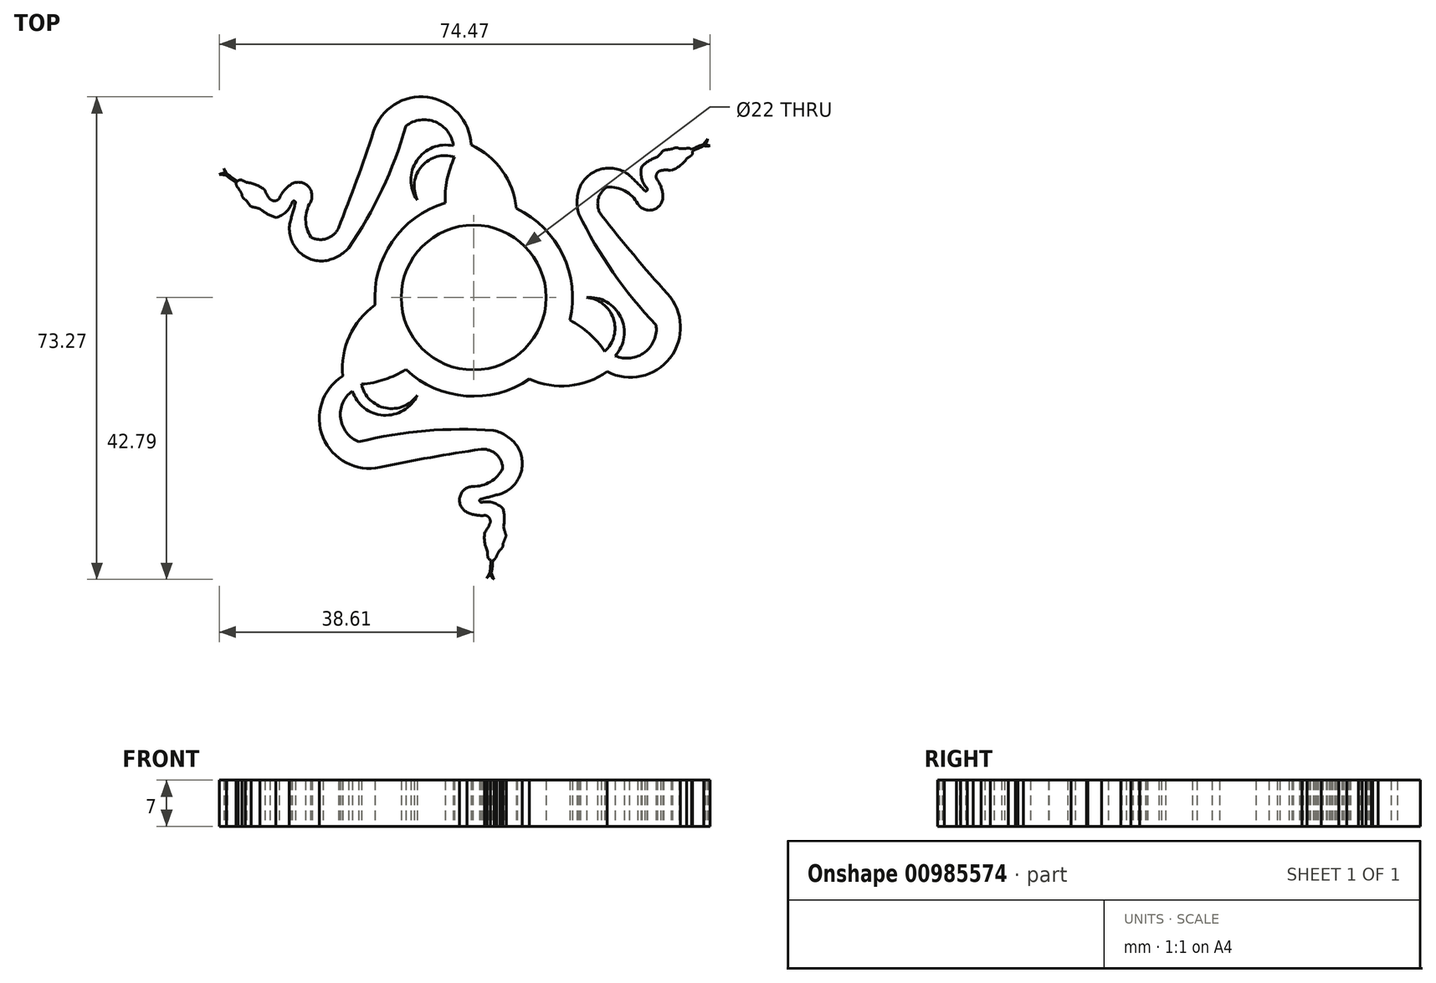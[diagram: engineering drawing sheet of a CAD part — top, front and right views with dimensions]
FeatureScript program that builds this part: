
annotation { "Feature Type Name" : "Feature", "Feature Type Description" : "" }
export const myFeature = defineFeature(function(context is Context, id is Id, definition is map)
    precondition{}
    {
        {
            var Q0;
            Q0=qCreatedBy(makeId("Top.planeOp"),FACE);
            var sketch = newSketch(context, id + "F0", { "sketchPlane" : qUnion([Q0])});
            skCircle(sketch, "E0", {"center": v(0, 0) * mm, "radius": 11 * mm});
            skCircle(sketch, "E1", {"center": v(0, 0) * mm, "radius": 43.5 * mm, "construction": true});
            skArc(sketch, "E2", {"start": v(19.91, -8.17) * mm, "mid": v(15.94, -4.24) * mm, "end": v(10.8, -2.07) * mm});
            skArc(sketch, "E3", {"start": v(19.91, -8.17) * mm, "mid": v(21.2, -3.17) * mm, "end": v(17.13, 0) * mm});
            skArc(sketch, "E4", {"start": v(21.5, -8.85) * mm, "mid": v(22.33, -2.94) * mm, "end": v(17.13, 0) * mm});
            skArc(sketch, "E5", {"start": v(21.5, -8.85) * mm, "mid": v(25.98, -8.32) * mm, "end": v(27.7, -4.15) * mm});
            skArc(sketch, "E6", {"start": v(15.98, 12.7) * mm, "mid": v(21.16, 3.81) * mm, "end": v(27.7, -4.15) * mm});
            skArc(sketch, "E7", {"start": v(16.21, 17) * mm, "mid": v(15.71, 14.87) * mm, "end": v(15.98, 12.7) * mm});
            skArc(sketch, "E8", {"start": v(23.64, 18.58) * mm, "mid": v(19.55, 19.54) * mm, "end": v(16.21, 17) * mm});
            skArc(sketch, "E9", {"start": v(26, 16.18) * mm, "mid": v(24.83, 17.4) * mm, "end": v(23.64, 18.58) * mm});
            skArc(sketch, "E10", {"start": v(26, 16.18) * mm, "mid": v(26.33, 16.3) * mm, "end": v(26.28, 16.64) * mm});
            skArc(sketch, "E11", {"start": v(25.52, 19.9) * mm, "mid": v(25.5, 18.18) * mm, "end": v(26.28, 16.64) * mm});
            skArc(sketch, "E12", {"start": v(27.87, 21.34) * mm, "mid": v(26.62, 20.75) * mm, "end": v(25.52, 19.9) * mm});
            skArc(sketch, "E13", {"start": v(27.87, 21.34) * mm, "mid": v(28.37, 21.84) * mm, "end": v(28.85, 22.36) * mm});
            skArc(sketch, "E14", {"start": v(30.18, 22.56) * mm, "mid": v(29.52, 22.46) * mm, "end": v(28.85, 22.36) * mm});
            skArc(sketch, "E15", {"start": v(31.17, 22.65) * mm, "mid": v(30.67, 22.75) * mm, "end": v(30.18, 22.56) * mm});
            skArc(sketch, "E16", {"start": v(31.17, 22.65) * mm, "mid": v(31.72, 22.6) * mm, "end": v(32.27, 22.65) * mm});
            skArc(sketch, "E17", {"start": v(33.12, 22.48) * mm, "mid": v(32.72, 22.66) * mm, "end": v(32.27, 22.65) * mm});
            skArc(sketch, "E18", {"start": v(34.85, 23.24) * mm, "mid": v(33.97, 22.9) * mm, "end": v(33.12, 22.48) * mm});
            skArc(sketch, "E19", {"start": v(34.85, 23.24) * mm, "mid": v(35.2, 23.65) * mm, "end": v(35.5, 24.09) * mm});
            skArc(sketch, "E20", {"start": v(35.17, 23.24) * mm, "mid": v(35.4, 23.63) * mm, "end": v(35.5, 24.09) * mm});
            skArc(sketch, "E21", {"start": v(35.86, 23.03) * mm, "mid": v(35.51, 23.14) * mm, "end": v(35.17, 23.24) * mm});
            skArc(sketch, "E22", {"start": v(34.93, 23.03) * mm, "mid": v(35.4, 23.02) * mm, "end": v(35.86, 23.03) * mm});
            skArc(sketch, "E23", {"start": v(33.22, 22.26) * mm, "mid": v(34.07, 22.64) * mm, "end": v(34.93, 23.03) * mm});
            skArc(sketch, "E24", {"start": v(33.12, 21.64) * mm, "mid": v(33.24, 21.94) * mm, "end": v(33.22, 22.26) * mm});
            skArc(sketch, "E25", {"start": v(32.35, 21.1) * mm, "mid": v(32.75, 21.36) * mm, "end": v(33.12, 21.64) * mm});
            skArc(sketch, "E26", {"start": v(30, 19.28) * mm, "mid": v(31.31, 20.01) * mm, "end": v(32.35, 21.1) * mm});
            skArc(sketch, "E27", {"start": v(30, 19.28) * mm, "mid": v(29.2, 19.36) * mm, "end": v(28.4, 19.28) * mm});
            skArc(sketch, "E28", {"start": v(28.4, 19.28) * mm, "mid": v(27.82, 18.83) * mm, "end": v(27.75, 18.1) * mm});
            skArc(sketch, "E29", {"start": v(28.73, 15.44) * mm, "mid": v(28.43, 16.84) * mm, "end": v(27.75, 18.1) * mm});
            skArc(sketch, "E30", {"start": v(24.91, 14.23) * mm, "mid": v(27.3, 13.35) * mm, "end": v(28.73, 15.44) * mm});
            skArc(sketch, "E31", {"start": v(24.91, 14.23) * mm, "mid": v(22.96, 16.18) * mm, "end": v(20.28, 16.8) * mm});
            skArc(sketch, "E32", {"start": v(20.28, 16.8) * mm, "mid": v(18.9, 14.84) * mm, "end": v(19.39, 12.5) * mm});
            skArc(sketch, "E33", {"start": v(19.39, 12.5) * mm, "mid": v(24.3, 6.46) * mm, "end": v(29.41, 0.57) * mm});
            skArc(sketch, "E34", {"start": v(20.28, -11.26) * mm, "mid": v(29.82, -9.18) * mm, "end": v(29.41, 0.57) * mm});
            skArc(sketch, "E35", {"start": v(8.3, -12.3) * mm, "mid": v(14.42, -13.4) * mm, "end": v(20.28, -11.26) * mm});
            skArc(sketch, "E36", {"start": v(4.32, -10.11) * mm, "mid": v(6.23, -11.34) * mm, "end": v(8.3, -12.3) * mm});
            skCircle(sketch, "E37", {"center": v(0, 0) * mm, "radius": 15 * mm});
            skSolve(sketch);
        }
        {
            var Q0;
            {var subQ0=sQuery(id+"F0.wireOp",EDGE,"E2");Q0=makeQuery(id+"F0.imprint","IMPRINT",FACE,{"disambiguationData":[TD([[makeQuery(id+"F0.imprint","IMPRINT",EDGE,{"derivedFrom":subQ0}),1.0]])]});}
            var Q1;
            {var subQ0=sQuery(id+"F0.wireOp",EDGE,"E3");Q1=makeQuery(id+"F0.imprint","IMPRINT",FACE,{"disambiguationData":[TD([[makeQuery(id+"F0.imprint","IMPRINT",EDGE,{"derivedFrom":subQ0}),-1.0]])]});}
            var Q2;
            {var subQ0=sQuery(id+"F0.wireOp",EDGE,"E36");Q2=makeQuery(id+"F0.imprint","IMPRINT",FACE,{"disambiguationData":[TD([[makeQuery(id+"F0.imprint","IMPRINT",EDGE,{"derivedFrom":subQ0}),-1.0]])]});}
            extrude(context, id + "F1", {"entities" : qUnion([Q0, Q1, Q2]), "depth" : 7 * mm, "offsetDistance" : 25 * mm});
        }
        {
            var Q0;
            Q0=makeQuery(id+"F1.opExtrude","SWEPT_BODY",BODY,{"disambiguationData":[OSD([sQuery(id+"F0.wireOp",EDGE,"E0"),sQuery(id+"F0.wireOp",EDGE,"E2"),sQuery(id+"F0.wireOp",EDGE,"E3"),sQuery(id+"F0.wireOp",EDGE,"E4"),sQuery(id+"F0.wireOp",EDGE,"E5"),sQuery(id+"F0.wireOp",EDGE,"E6"),sQuery(id+"F0.wireOp",EDGE,"E7"),sQuery(id+"F0.wireOp",EDGE,"E8"),sQuery(id+"F0.wireOp",EDGE,"E9"),sQuery(id+"F0.wireOp",EDGE,"E10"),sQuery(id+"F0.wireOp",EDGE,"E11"),sQuery(id+"F0.wireOp",EDGE,"E12"),sQuery(id+"F0.wireOp",EDGE,"E13"),sQuery(id+"F0.wireOp",EDGE,"E14"),sQuery(id+"F0.wireOp",EDGE,"E15"),sQuery(id+"F0.wireOp",EDGE,"E16"),sQuery(id+"F0.wireOp",EDGE,"E17"),sQuery(id+"F0.wireOp",EDGE,"E18"),sQuery(id+"F0.wireOp",EDGE,"E19"),sQuery(id+"F0.wireOp",EDGE,"E20"),sQuery(id+"F0.wireOp",EDGE,"E21"),sQuery(id+"F0.wireOp",EDGE,"E22"),sQuery(id+"F0.wireOp",EDGE,"E23"),sQuery(id+"F0.wireOp",EDGE,"E24"),sQuery(id+"F0.wireOp",EDGE,"E25"),sQuery(id+"F0.wireOp",EDGE,"E26"),sQuery(id+"F0.wireOp",EDGE,"E27"),sQuery(id+"F0.wireOp",EDGE,"E28"),sQuery(id+"F0.wireOp",EDGE,"E29"),sQuery(id+"F0.wireOp",EDGE,"E30"),sQuery(id+"F0.wireOp",EDGE,"E31"),sQuery(id+"F0.wireOp",EDGE,"E32"),sQuery(id+"F0.wireOp",EDGE,"E33"),sQuery(id+"F0.wireOp",EDGE,"E34"),sQuery(id+"F0.wireOp",EDGE,"E35"),sQuery(id+"F0.wireOp",EDGE,"E37")])]});
            var Q1;
            Q1=sQuery(id+"F0.wireOp",EDGE,"E0");
            circularPattern(context, id + "F2", {"operationType" : NewBodyOperationType.ADD, "entities" : qUnion([Q0]), "axis" : qUnion([Q1]), "angle" : 360 * degree, "instanceCount" : 3, "equalSpace" : true});
        }
    });
